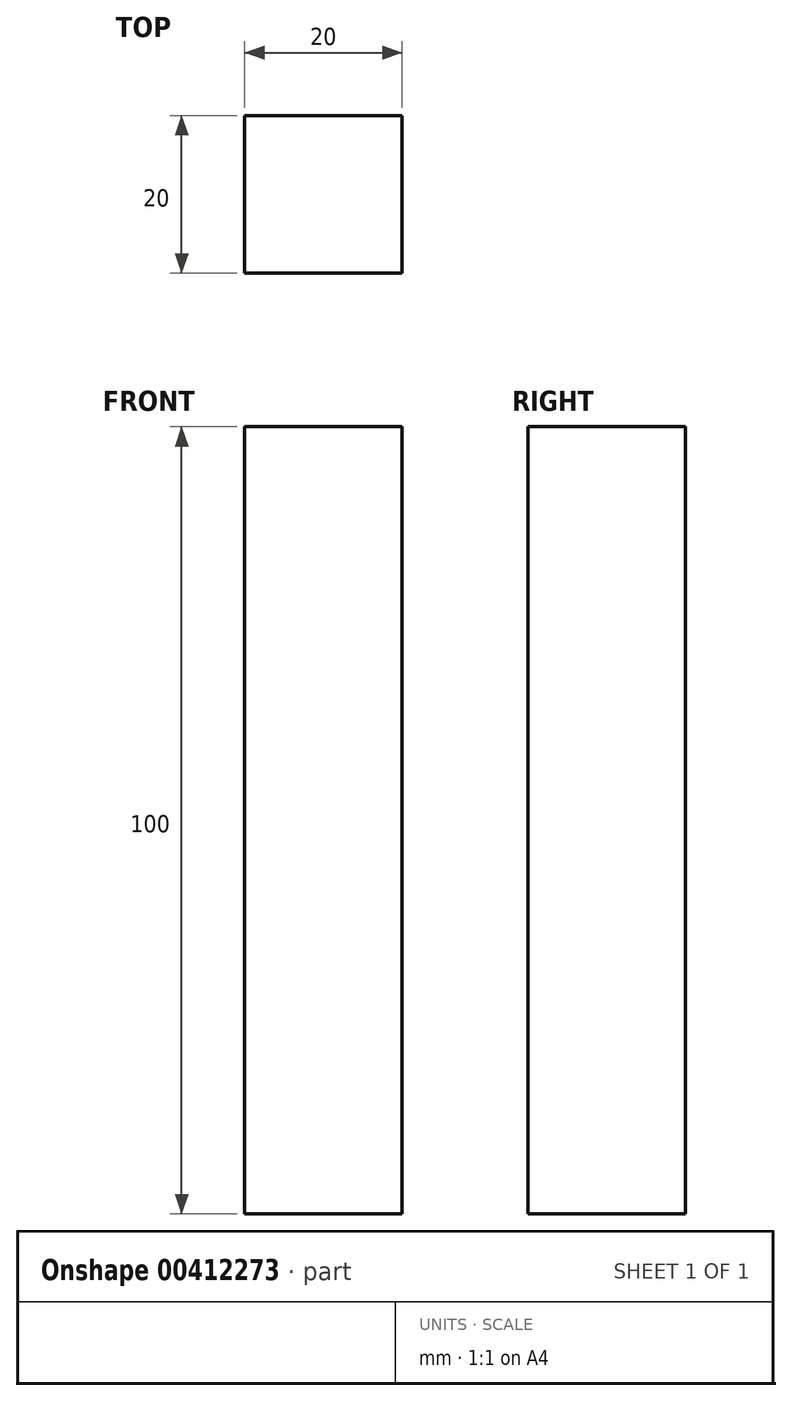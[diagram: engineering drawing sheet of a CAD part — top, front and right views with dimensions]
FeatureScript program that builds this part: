
annotation { "Feature Type Name" : "Feature", "Feature Type Description" : "" }
export const myFeature = defineFeature(function(context is Context, id is Id, definition is map)
    precondition{}
    {
        {
            var Q0;
            Q0=qCreatedBy(makeId("Front.planeOp"),FACE);
            var sketch = newSketch(context, id + "F0", { "sketchPlane" : qUnion([Q0])});
            skLineSegment(sketch, "E0.bottom", {"start": v(0, 0) * mm, "end": v(20, 0) * mm});
            skLineSegment(sketch, "E0.top", {"start": v(0, 100) * mm, "end": v(20, 100) * mm});
            skLineSegment(sketch, "E0.left", {"start": v(0, 0) * mm, "end": v(0, 100) * mm});
            skLineSegment(sketch, "E0.right", {"start": v(20, 0) * mm, "end": v(20, 100) * mm});
            skSolve(sketch);
        }
        {
            var Q0;
            Q0=makeQuery(id+"F0.imprint","IMPRINT",FACE,{"disambiguationData":[TD([[makeQuery(id+"F0.imprint","IMPRINT",EDGE,{"derivedFrom":sQuery(id+"F0.wireOp",EDGE,"E0.bottom")}),1.0]])]});
            extrude(context, id + "F1", {"entities" : qUnion([Q0]), "depth" : 20 * mm});
        }
    });
